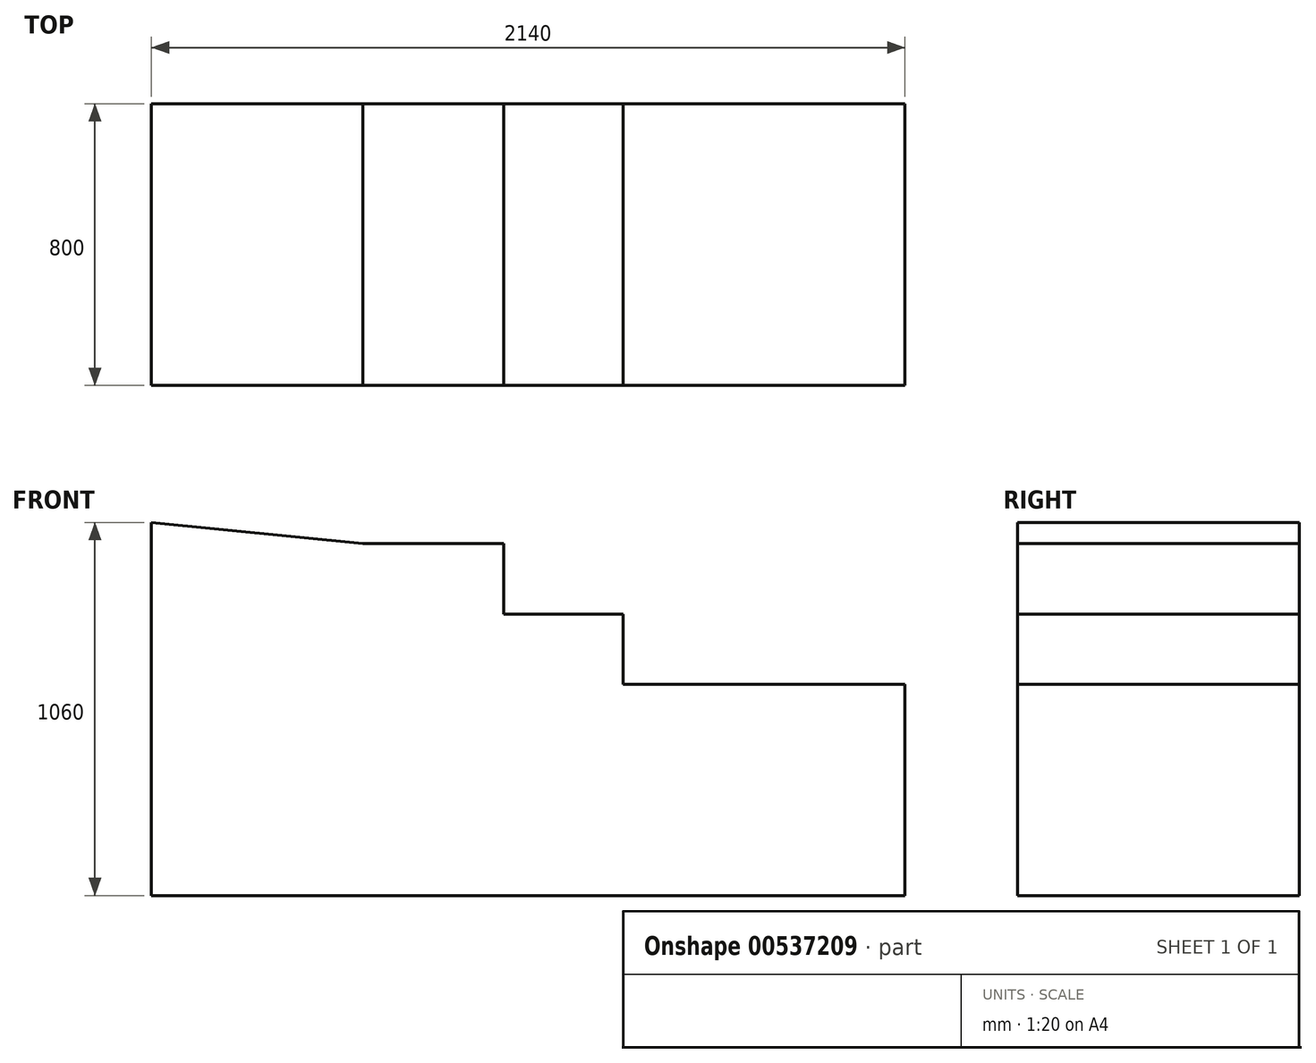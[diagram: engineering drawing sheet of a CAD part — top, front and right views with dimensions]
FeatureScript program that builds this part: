
annotation { "Feature Type Name" : "Feature", "Feature Type Description" : "" }
export const myFeature = defineFeature(function(context is Context, id is Id, definition is map)
    precondition{}
    {
        {
            var Q0;
            Q0=qCreatedBy(makeId("Front.planeOp"),FACE);
            var sketch = newSketch(context, id + "F0", { "sketchPlane" : qUnion([Q0])});
            skLineSegment(sketch, "E0", {"start": v(0, 0) * mm, "end": v(0, 200) * mm});
            skLineSegment(sketch, "E1", {"start": v(0, 200) * mm, "end": v(-340, 200) * mm});
            skLineSegment(sketch, "E2", {"start": v(-340, 200) * mm, "end": v(-340, 400) * mm});
            skLineSegment(sketch, "E3", {"start": v(-340, 400) * mm, "end": v(-740, 400) * mm});
            skLineSegment(sketch, "E4", {"start": v(-740, 400) * mm, "end": v(-1340, 460) * mm});
            skLineSegment(sketch, "E5", {"start": v(-1340, 460) * mm, "end": v(-1340, -600) * mm});
            skLineSegment(sketch, "E6", {"start": v(-1340, -600) * mm, "end": v(800, -600) * mm});
            skLineSegment(sketch, "E7", {"start": v(800, -600) * mm, "end": v(800, 0) * mm});
            skLineSegment(sketch, "E8", {"start": v(800, 0) * mm, "end": v(0, 0) * mm});
            skSolve(sketch);
        }
        {
            var Q0;
            Q0=makeQuery(id+"F0.imprint","IMPRINT",FACE,{"disambiguationData":[TD([[makeQuery(id+"F0.imprint","IMPRINT",EDGE,{"derivedFrom":sQuery(id+"F0.wireOp",EDGE,"E0")}),1.0]])]});
            extrude(context, id + "F1", {"entities" : qUnion([Q0]), "depth" : 800 * mm, "offsetDistance" : 25 * mm});
        }
    });
